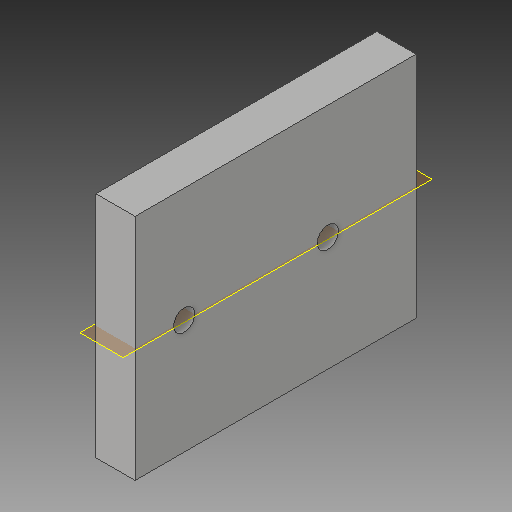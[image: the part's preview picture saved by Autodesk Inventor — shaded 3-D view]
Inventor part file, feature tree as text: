
AUTODESK INVENTOR PART (.ipt)
format: ipt  version: 2018 (Build 220112000, 112)  size: 113,152 bytes
history: native  units: mm
features: reference x5, extrude x4, sketch x4, thread x2, plane x1
ambient origin geometry x8: Origin, YZ Plane, XZ Plane, XY Plane, X Axis, Y Axis, Z Axis, Center Point
bodies: Solid1 (feature_tree)
feature tree (16):
  extrude  "Extrusion1"  Depth=70.0mm
  plane  "Work Plane1"
  extrude  "Extrusion2"  Depth=12.0mm
  extrude  "Extrusion3"  Depth=25.0mm
  extrude  "Extrusion4"  Depth=15.0mm TaperAngle=0.0deg
  thread  "Thread1"  [1 undecoded]
  thread  "Thread2"  [1 undecoded]
  sketch  "Sketch1"  dims[d0=86.0mm d1=70.0mm]
  sketch  "Sketch2"  dims[d2=12.0mm d3=0.0mm d4=6.0mm]
  sketch  "Sketch3"  dims[d5=25.0mm d6=25.0mm]
  reference  "Reference1"
  reference  "Reference2"
  reference  "Reference3"
  sketch  "Sketch4"  dims[d7=15.0mm d8=0.0mm d9=15.0mm d10=0.0mm d11=10.0mm d12=0.0mm d13=0.25mm d14=0.25mm d15=10.0mm d16=0.0mm d17=10.0mm d18=0.0mm]
  reference  "Reference4"
  reference  "Reference5"
note: 2 required parameter values undecoded (feature->parameter linkage not recoverable at this tier; creation-order binding heuristic only, values carry confidence <= 0.55)
